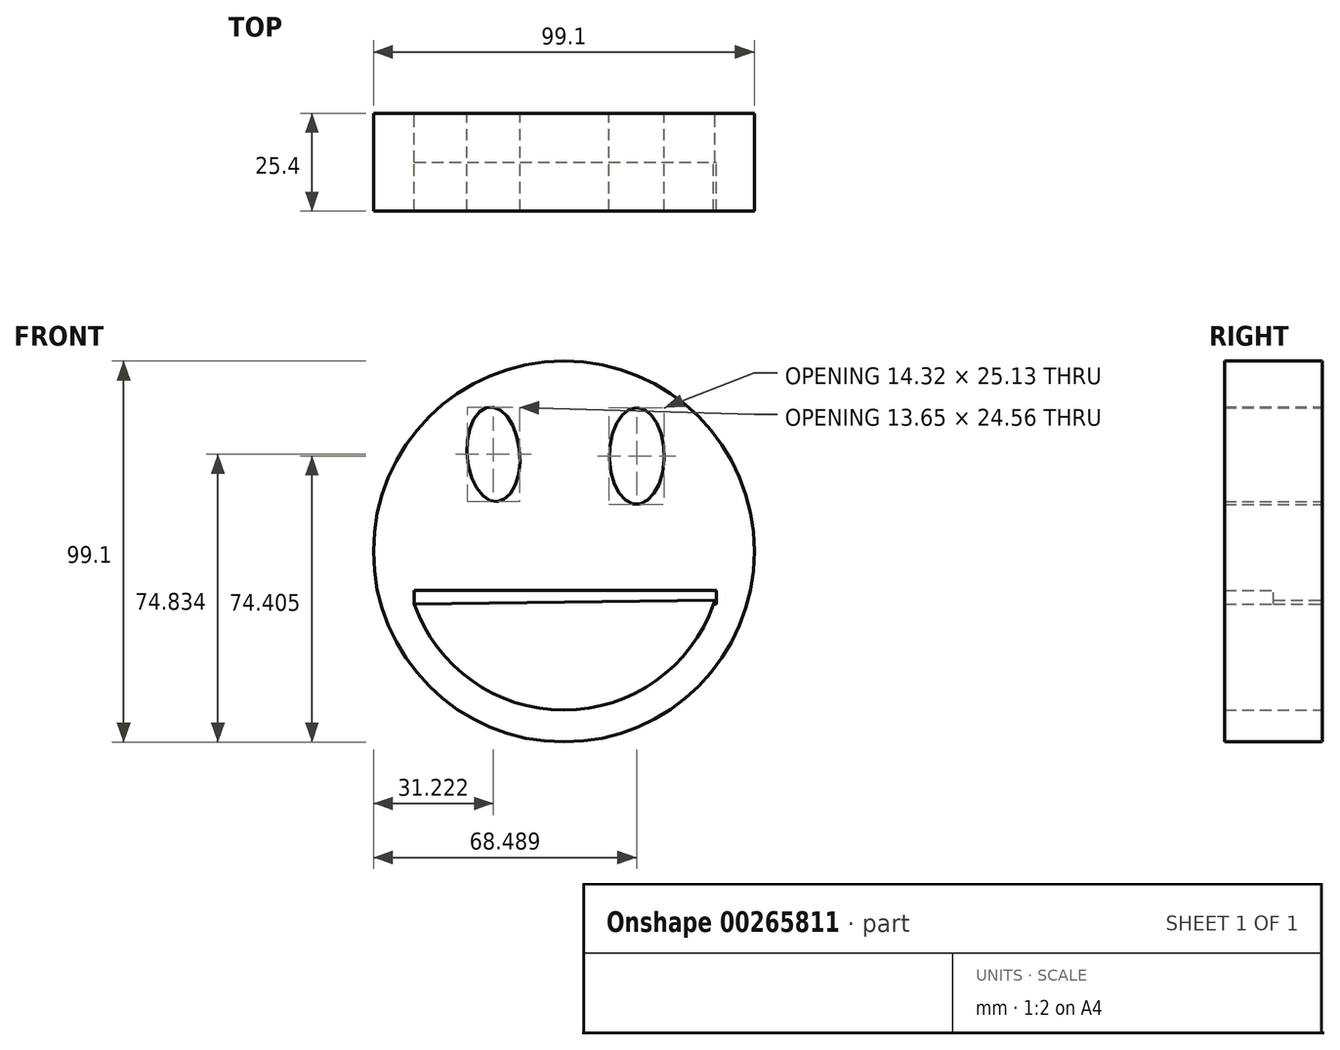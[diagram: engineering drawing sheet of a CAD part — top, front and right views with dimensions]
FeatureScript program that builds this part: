
annotation { "Feature Type Name" : "Feature", "Feature Type Description" : "" }
export const myFeature = defineFeature(function(context is Context, id is Id, definition is map)
    precondition{}
    {
        {
            var Q0;
            Q0=qCreatedBy(makeId("Front.planeOp"),FACE);
            var sketch = newSketch(context, id + "F0", { "sketchPlane" : qUnion([Q0])});
            skCircle(sketch, "E0", {"center": v(0, 0) * mm, "radius": 49.55 * mm});
            skArc(sketch, "E1", {"start": v(39.3, -12.6) * mm, "mid": v(0.56, -41.26) * mm, "end": v(-38.94, -13.66) * mm});
            skLineSegment(sketch, "E2", {"start": v(-38.94, -13.66) * mm, "end": v(39.3, -12.6) * mm});
            skEllipse(sketch, "E3", {"center": v(-18.33, 25.28) * mm, "majorRadius": 12.32 * mm, "minorRadius": 6.85 * mm, "majorAxis": v(0.08, -1)});
            skEllipse(sketch, "E4", {"center": v(18.94, 24.86) * mm, "majorRadius": 12.57 * mm, "minorRadius": 7.16 * mm, "majorAxis": v(0, 1)});
            skLineSegment(sketch, "E5.bottom", {"start": v(-38.94, -13.66) * mm, "end": v(39.7, -13.66) * mm});
            skLineSegment(sketch, "E5.top", {"start": v(-38.94, -10.07) * mm, "end": v(39.7, -10.07) * mm});
            skLineSegment(sketch, "E5.left", {"start": v(-38.94, -13.66) * mm, "end": v(-38.94, -10.07) * mm});
            skLineSegment(sketch, "E5.right", {"start": v(39.7, -13.66) * mm, "end": v(39.7, -10.07) * mm});
            skSolve(sketch);
        }
        {
            var Q0;
            Q0=makeQuery(id+"F0.imprint","IMPRINT",FACE,{"disambiguationData":[TD([[makeQuery(id+"F0.imprint","IMPRINT",EDGE,{"derivedFrom":sQuery(id+"F0.wireOp",EDGE,"E0")}),1.0]])]});
            extrude(context, id + "F1", {"entities" : qUnion([Q0]), "depth" : 25.4 * mm});
        }
        {
            var Q0;
            {var subQ0=sQuery(id+"F0.wireOp",EDGE,"E5.bottom");var subQ1=sQuery(id+"F0.wireOp",EDGE,"E1");var subQ3=makeQuery(id+"F0.imprint","INTERSECT",VERTEX,{"derivedFrom":[subQ1,subQ0]});Q0=makeQuery(id+"F0.imprint","IMPRINT",FACE,{"disambiguationData":[TD([[makeQuery(id+"F0.imprint","IMPRINT",EDGE,{"disambiguationData":[TD([[subQ3,-1.0]])],"derivedFrom":subQ1}),-1.0]])]});}
            extrude(context, id + "F2", {"entities" : qUnion([Q0]), "operationType" : NewBodyOperationType.ADD, "depth" : 12.7 * mm});
        }
        {
            var Q0;
            {var subQ0=sQuery(id+"F0.wireOp",EDGE,"E2");Q0=makeQuery(id+"F0.imprint","IMPRINT",FACE,{"disambiguationData":[TD([[makeQuery(id+"F0.imprint","IMPRINT",EDGE,{"derivedFrom":subQ0}),1.0]])]});}
            extrude(context, id + "F3", {"entities" : qUnion([Q0]), "operationType" : NewBodyOperationType.ADD, "depth" : 12.7 * mm});
        }
    });
